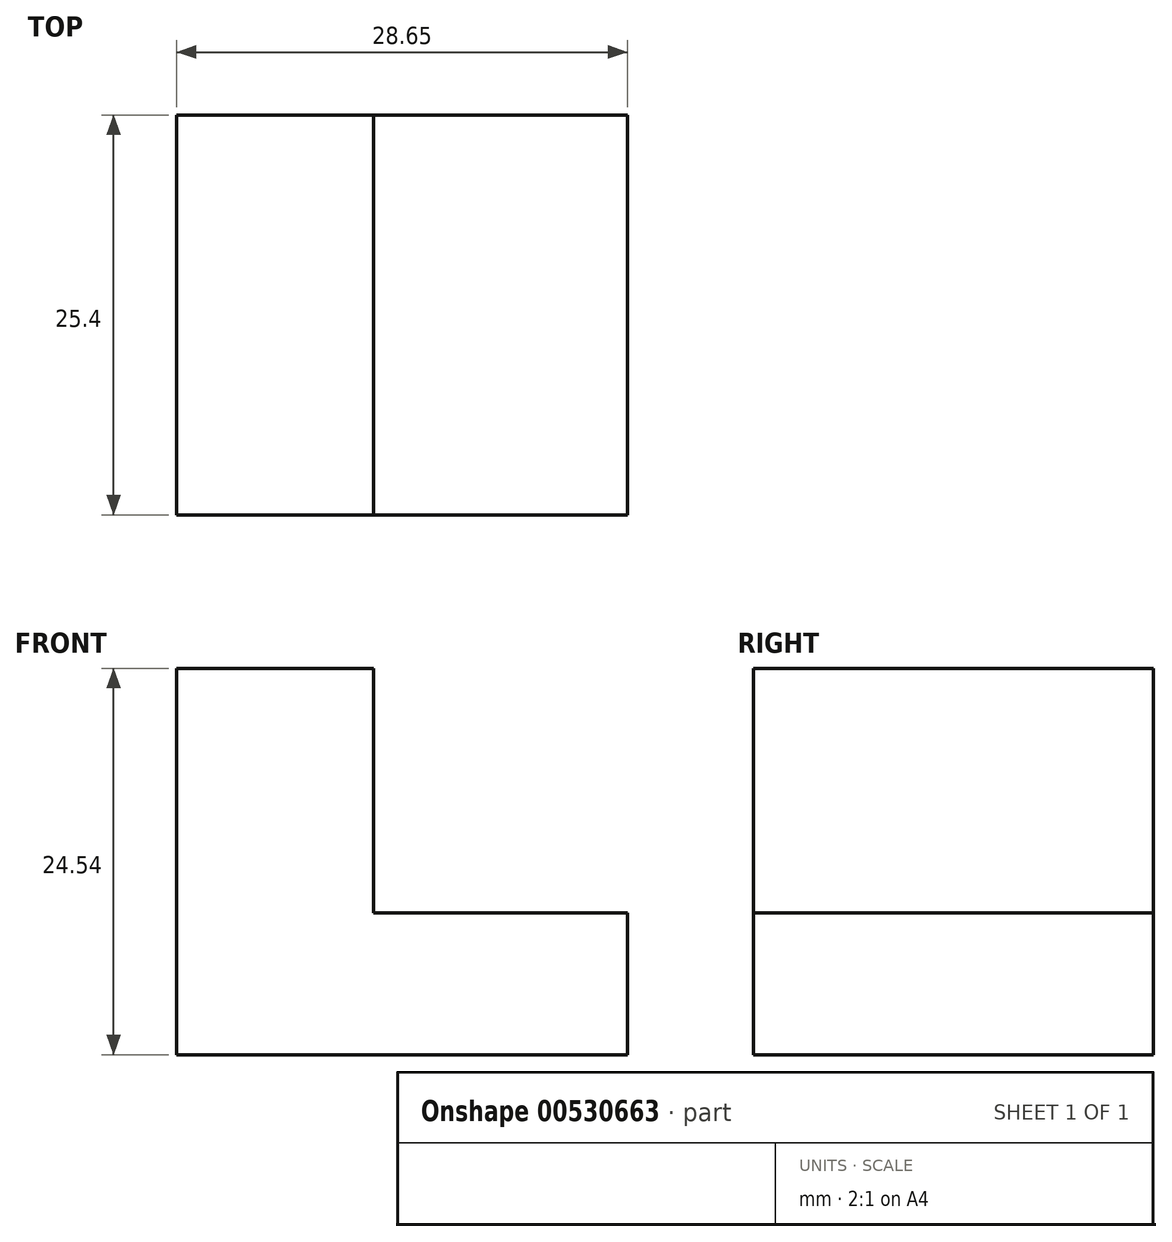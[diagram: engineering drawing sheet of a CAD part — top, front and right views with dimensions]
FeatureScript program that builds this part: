
annotation { "Feature Type Name" : "Feature", "Feature Type Description" : "" }
export const myFeature = defineFeature(function(context is Context, id is Id, definition is map)
    precondition{}
    {
        {
            var Q0;
            Q0=qCreatedBy(makeId("Front.planeOp"),FACE);
            var sketch = newSketch(context, id + "F0", { "sketchPlane" : qUnion([Q0])});
            skLineSegment(sketch, "E0", {"start": v(0, 0) * mm, "end": v(0, 24.54) * mm});
            skLineSegment(sketch, "E1", {"start": v(0, 24.54) * mm, "end": v(12.5, 24.54) * mm});
            skLineSegment(sketch, "E2", {"start": v(12.5, 24.54) * mm, "end": v(12.5, 9) * mm});
            skLineSegment(sketch, "E3", {"start": v(12.5, 9) * mm, "end": v(28.65, 9) * mm});
            skLineSegment(sketch, "E4", {"start": v(28.65, 9) * mm, "end": v(28.65, 0) * mm});
            skLineSegment(sketch, "E5", {"start": v(28.65, 0) * mm, "end": v(0, 0) * mm});
            skSolve(sketch);
        }
        {
            var Q0;
            Q0=makeQuery(id+"F0.imprint","IMPRINT",FACE,{"disambiguationData":[TD([[makeQuery(id+"F0.imprint","IMPRINT",EDGE,{"derivedFrom":sQuery(id+"F0.wireOp",EDGE,"E0")}),-1.0]])]});
            extrude(context, id + "F1", {"entities" : qUnion([Q0]), "depth" : 25.4 * mm, "offsetDistance" : 25.4 * mm});
        }
    });
